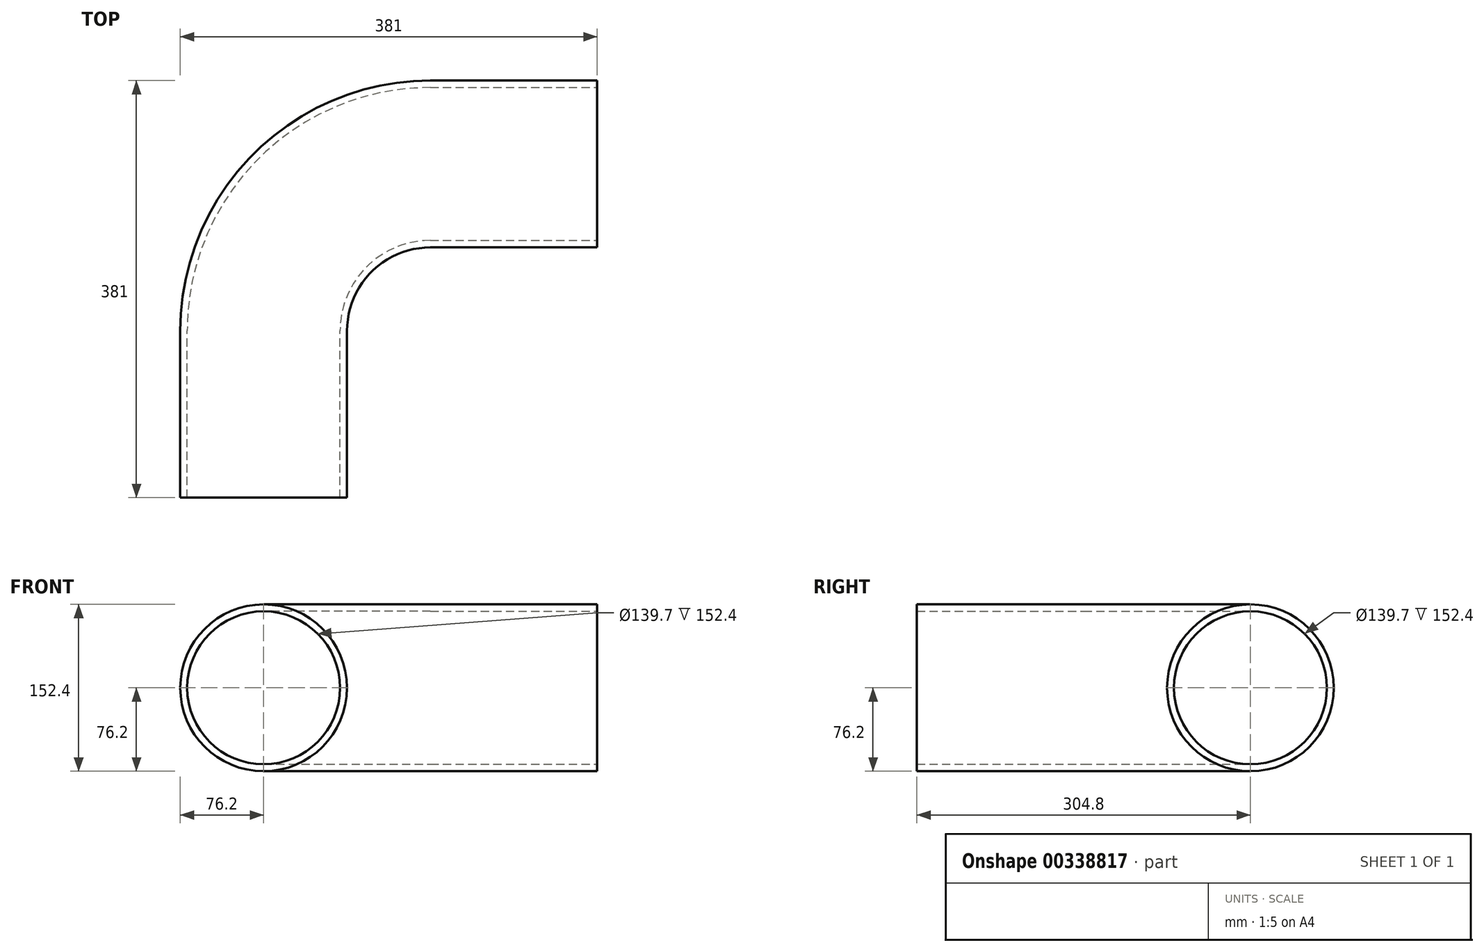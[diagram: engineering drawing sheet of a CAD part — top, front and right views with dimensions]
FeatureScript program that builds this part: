
annotation { "Feature Type Name" : "Feature", "Feature Type Description" : "" }
export const myFeature = defineFeature(function(context is Context, id is Id, definition is map)
    precondition{}
    {
        {
            var Q0;
            Q0=qCreatedBy(makeId("Front.planeOp"),FACE);
            var sketch = newSketch(context, id + "F0", { "sketchPlane" : qUnion([Q0])});
            skCircle(sketch, "E0", {"center": v(0, 0) * mm, "radius": 76.2 * mm});
            skSolve(sketch);
        }
        {
            var Q0;
            Q0=qCreatedBy(makeId("Top.planeOp"),FACE);
            var sketch = newSketch(context, id + "F1", { "sketchPlane" : qUnion([Q0])});
            skLineSegment(sketch, "E1", {"start": v(0, 0) * mm, "end": v(0, 152.4) * mm});
            skLineSegment(sketch, "E2", {"start": v(152.4, 304.8) * mm, "end": v(304.8, 304.8) * mm});
            skPoint(sketch, "E3.visualSharp", {"position": v(0, 304.8) * mm});
            skArc(sketch, "E3.filletArc", {"start": v(152.4, 304.8) * mm, "mid": v(44.64, 260.16) * mm, "end": v(0, 152.4) * mm});
            skSolve(sketch);
        }
        {
            var Q0;
            Q0=makeQuery(id+"F0.imprint","IMPRINT",FACE,{"disambiguationData":[TD([[makeQuery(id+"F0.imprint","IMPRINT",EDGE,{"derivedFrom":sQuery(id+"F0.wireOp",EDGE,"E0")}),1.0]])]});
            var Q1;
            Q1=sQuery(id+"F1.wireOp",EDGE,"E1");
            var Q2;
            Q2=sQuery(id+"F1.wireOp",EDGE,"E3.filletArc");
            var Q3;
            Q3=sQuery(id+"F1.wireOp",EDGE,"E2");
            sweep(context, id + "F2", {"profiles" : qUnion([Q0]), "path" : qUnion([Q1, Q2, Q3])});
        }
        {
            var Q0;
            Q0=makeQuery(id+"F2.opSweep","CAP_FACE",FACE,{"disambiguationData":[OSD([sQuery(id+"F0.wireOp",EDGE,"E0"),sQuery(id+"F1.wireOp",VERTEX,"E1.start")])],"isStart":true});
            var Q1;
            Q1=makeQuery(id+"F2.opSweep","CAP_FACE",FACE,{"disambiguationData":[OSD([sQuery(id+"F0.wireOp",EDGE,"E0"),sQuery(id+"F1.wireOp",VERTEX,"E2.end")])],"isStart":false});
            var Q2;
            Q2=makeQuery(id+"F2.opSweep","SWEPT_BODY",BODY,{"disambiguationData":[OSD([sQuery(id+"F0.wireOp",EDGE,"E0"),sQuery(id+"F1.wireOp",EDGE,"E2")])]});
            shell(context, id + "F3", {"entities" : qUnion([Q0, Q1]), "parts" : qUnion([Q2]), "thickness" : 6.35 * mm});
        }
    });
